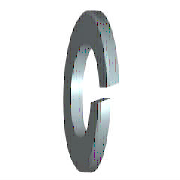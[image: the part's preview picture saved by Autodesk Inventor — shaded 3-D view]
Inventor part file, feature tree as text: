
AUTODESK INVENTOR PART (.ipt)
format: ipt  version: 2020 (Build 240168000, 168)  size: 125,952 bytes
history: native  units: mm (DEFAULTED — no unit token found)
features: extrude x2, sketch x2, other x1, plane x1
ambient origin geometry x6: Origin, YZ Plane, X Axis, Y Axis, Z Axis, Center Point
bodies: Solid1 (feature_tree)
feature tree (6):
  extrude  "轴承体"  Depth=18.4mm
  extrude  "切口"  TaperAngle=0.0deg  [1 undecoded]
  other  "Work Axis1"
  plane  "Work Plane1"
  sketch  "草图1"  dims[d0=12.2mm d1=18.4mm]
  sketch  "草图2"  dims[d2=3.1mm d3=0.0mm d4=0.62mm d5=0.62mm d6=12.566371mm d7=3.1mm d8=0.0mm d9=0.0mm d10=0.0mm d11=0.0mm d12=0.0mm]
note: 1 required parameter value undecoded (feature->parameter linkage not recoverable at this tier; creation-order binding heuristic only, values carry confidence <= 0.55)
